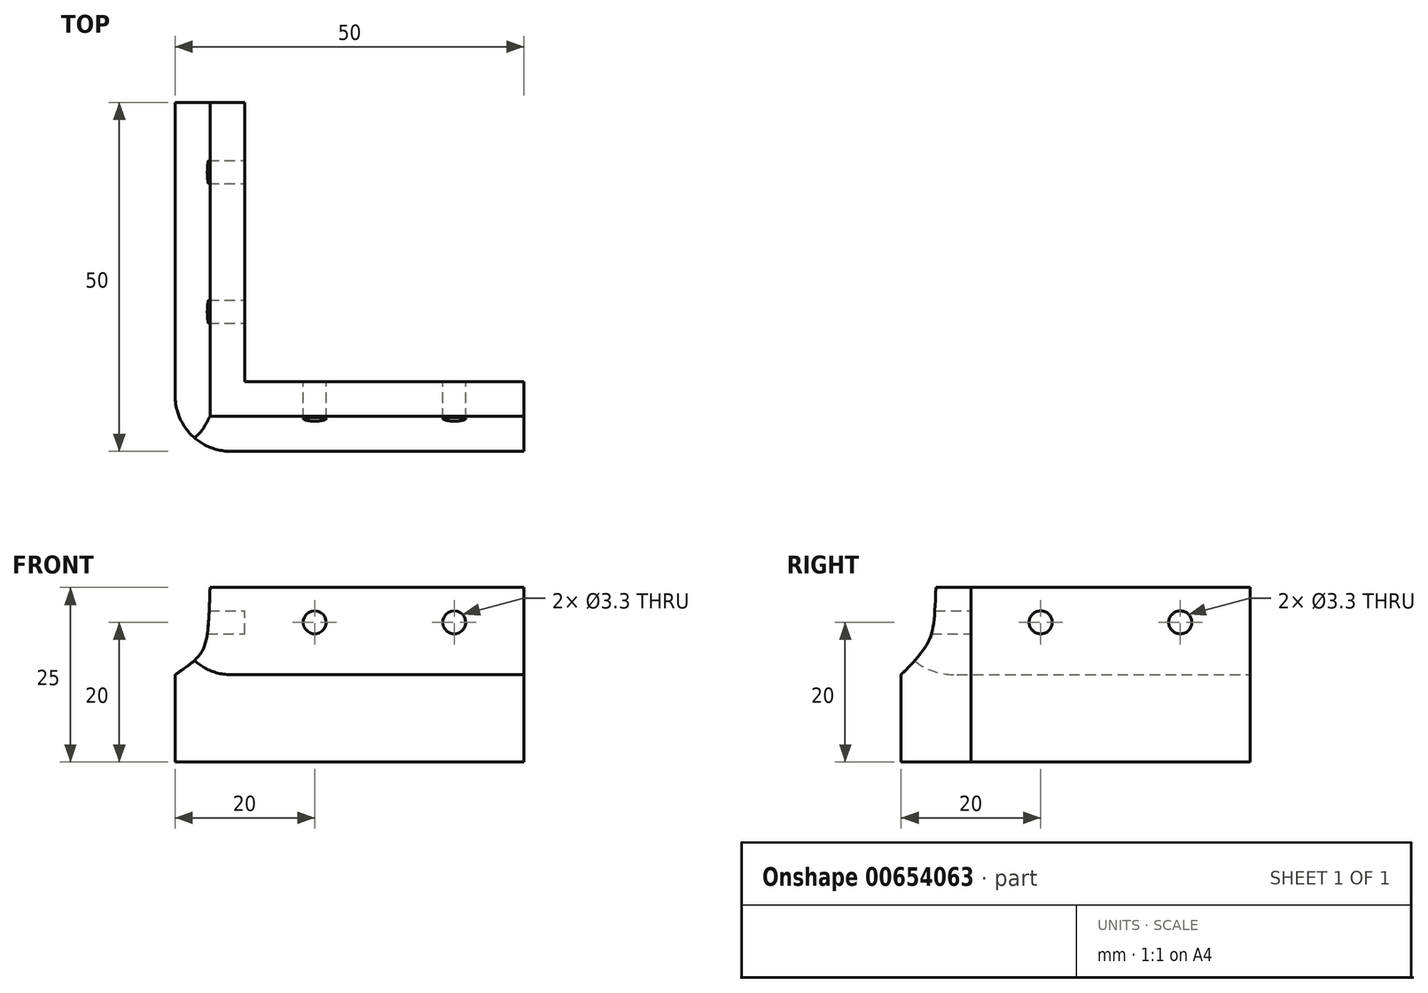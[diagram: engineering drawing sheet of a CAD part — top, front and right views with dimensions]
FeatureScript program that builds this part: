
annotation { "Feature Type Name" : "Feature", "Feature Type Description" : "" }
export const myFeature = defineFeature(function(context is Context, id is Id, definition is map)
    precondition{}
    {
        {
            var Q0;
            Q0=qCreatedBy(makeId("Top.planeOp"),FACE);
            var sketch = newSketch(context, id + "F0", { "sketchPlane" : qUnion([Q0])});
            skLineSegment(sketch, "E0", {"start": v(0, 8) * mm, "end": v(0, 50) * mm});
            skLineSegment(sketch, "E1", {"start": v(0, 50) * mm, "end": v(10, 50) * mm});
            skLineSegment(sketch, "E2", {"start": v(10, 50) * mm, "end": v(10, 10) * mm});
            skLineSegment(sketch, "E3", {"start": v(10, 10) * mm, "end": v(50, 10) * mm});
            skLineSegment(sketch, "E4", {"start": v(50, 10) * mm, "end": v(50, 0) * mm});
            skLineSegment(sketch, "E5", {"start": v(50, 0) * mm, "end": v(8, 0) * mm});
            skPoint(sketch, "E6.visualSharp", {"position": v(0, 0) * mm});
            skArc(sketch, "E6.filletArc", {"start": v(0, 8) * mm, "mid": v(2.34, 2.34) * mm, "end": v(8, 0) * mm});
            skSolve(sketch);
        }
        {
            var Q0;
            Q0=makeQuery(id+"F0.imprint","IMPRINT",FACE,{"disambiguationData":[TD([[makeQuery(id+"F0.imprint","IMPRINT",EDGE,{"derivedFrom":sQuery(id+"F0.wireOp",EDGE,"E0")}),-1.0]])]});
            extrude(context, id + "F1", {"entities" : qUnion([Q0]), "depth" : 25 * mm, "offsetDistance" : 25 * mm});
        }
        {
            var Q0;
            Q0=makeQuery(id+"F1.opExtrude","SWEPT_FACE",FACE,{"disambiguationData":[OSD([sQuery(id+"F0.wireOp",EDGE,"E4")])]});
            var sketch = newSketch(context, id + "F2", { "sketchPlane" : qUnion([Q0])});
            skFitSpline(sketch, "E7", {"points": [v(5, 25) * mm, v(0, 12.5) * mm], "startDerivative": vector(-1.04, -22.5) * mm, "endDerivative": vector(-14.09, -14.54) * mm});
            skSolve(sketch);
        }
        {
            var Q0;
            {var subQ0=sQuery(id+"F2.wireOp",EDGE,"E7");Q0=makeQuery(id+"F2.imprint","IMPRINT",FACE,{"disambiguationData":[TD([[makeQuery(id+"F2.imprint","IMPRINT",EDGE,{"derivedFrom":subQ0}),-1.0]])]});}
            extrude(context, id + "F3", {"entities" : qUnion([Q0]), "operationType" : NewBodyOperationType.REMOVE, "endBound" : BoundingType.THROUGH_ALL, "oppositeDirection" : true, "depth" : 25 * mm, "offsetDistance" : 25 * mm});
        }
        {
            var Q0;
            Q0=makeQuery(id+"F1.opExtrude","SWEPT_FACE",FACE,{"disambiguationData":[OSD([sQuery(id+"F0.wireOp",EDGE,"E1")])]});
            var sketch = newSketch(context, id + "F4", { "sketchPlane" : qUnion([Q0])});
            skFitSpline(sketch, "E8", {"points": [v(-5, 25) * mm, v(0, 12.5) * mm], "startDerivative": vector(0.95, -27.95) * mm, "endDerivative": vector(14.05, -9.55) * mm});
            skSolve(sketch);
        }
        {
            var Q0;
            {var subQ0=sQuery(id+"F4.wireOp",EDGE,"E8");Q0=makeQuery(id+"F4.imprint","IMPRINT",FACE,{"disambiguationData":[TD([[makeQuery(id+"F4.imprint","IMPRINT",EDGE,{"derivedFrom":subQ0}),1.0]])]});}
            extrude(context, id + "F5", {"entities" : qUnion([Q0]), "operationType" : NewBodyOperationType.REMOVE, "endBound" : BoundingType.THROUGH_ALL, "oppositeDirection" : true, "depth" : 25 * mm, "offsetDistance" : 25 * mm});
        }
        {
            var Q0;
            Q0=makeQuery(id+"F1.opExtrude","SWEPT_FACE",FACE,{"disambiguationData":[OSD([sQuery(id+"F0.wireOp",EDGE,"E3")])]});
            var sketch = newSketch(context, id + "F6", { "sketchPlane" : qUnion([Q0])});
            skPoint(sketch, "E9", {"position": v(-20, 20) * mm});
            skPoint(sketch, "E10", {"position": v(-40, 20) * mm});
            skSolve(sketch);
        }
        {
            var Q0;
            Q0=sQuery(id+"F6.wireOp",VERTEX,"E10");
            var Q1;
            Q1=sQuery(id+"F6.wireOp",VERTEX,"E9");
            var Q2;
            Q2=makeQuery(id+"F1.opExtrude","SWEPT_BODY",BODY,{"disambiguationData":[OSD([sQuery(id+"F0.wireOp",EDGE,"E0"),sQuery(id+"F0.wireOp",EDGE,"E1"),sQuery(id+"F0.wireOp",EDGE,"E2"),sQuery(id+"F0.wireOp",EDGE,"E3"),sQuery(id+"F0.wireOp",EDGE,"E4"),sQuery(id+"F0.wireOp",EDGE,"E5"),sQuery(id+"F0.wireOp",EDGE,"E6.filletArc")])]});
            hole(context, id + "F7", {"style" : HoleStyle.SIMPLE, "endStyle" : HoleEndStyle.THROUGH, "standardTappedOrClearance" : lookupTablePath({ "standard" : "ISO", "fit" : "Normal", "size" : "M3", "type" : "Clearance" }), "standardBlindInLast" : lookupTablePath({ "fit" : "Standard", "standard" : "ISO", "size" : "M3", "type" : "Clearance" }), "holeDiameter" : 3.3 * mm, "majorDiameter" : 3 * mm, "isTappedThrough" : true, "tappedDepth" : 5 * mm, "tapClearance" : 3, "startFromSketch" : true, "locations" : qUnion([Q0, Q1]), "scope" : qUnion([Q2])});
        }
        {
            var Q0;
            Q0=makeQuery(id+"F1.opExtrude","SWEPT_FACE",FACE,{"disambiguationData":[OSD([sQuery(id+"F0.wireOp",EDGE,"E2")])]});
            var sketch = newSketch(context, id + "F8", { "sketchPlane" : qUnion([Q0])});
            skPoint(sketch, "E11", {"position": v(20, 20) * mm});
            skPoint(sketch, "E12", {"position": v(40, 20) * mm});
            skSolve(sketch);
        }
        {
            var Q0;
            Q0=sQuery(id+"F8.wireOp",VERTEX,"E11");
            var Q1;
            Q1=sQuery(id+"F8.wireOp",VERTEX,"E12");
            var Q2;
            Q2=makeQuery(id+"F1.opExtrude","SWEPT_BODY",BODY,{"disambiguationData":[OSD([sQuery(id+"F0.wireOp",EDGE,"E0"),sQuery(id+"F0.wireOp",EDGE,"E1"),sQuery(id+"F0.wireOp",EDGE,"E2"),sQuery(id+"F0.wireOp",EDGE,"E3"),sQuery(id+"F0.wireOp",EDGE,"E4"),sQuery(id+"F0.wireOp",EDGE,"E5"),sQuery(id+"F0.wireOp",EDGE,"E6.filletArc")])]});
            hole(context, id + "F9", {"style" : HoleStyle.SIMPLE, "endStyle" : HoleEndStyle.THROUGH, "standardTappedOrClearance" : lookupTablePath({ "standard" : "ISO", "fit" : "Normal", "size" : "M3", "type" : "Clearance" }), "standardBlindInLast" : lookupTablePath({ "fit" : "Standard", "standard" : "ISO", "size" : "M3", "type" : "Clearance" }), "holeDiameter" : 3.3 * mm, "majorDiameter" : 5 * mm, "isTappedThrough" : true, "tappedDepth" : 5 * mm, "tapClearance" : 3, "startFromSketch" : true, "locations" : qUnion([Q0, Q1]), "scope" : qUnion([Q2])});
        }
    });
